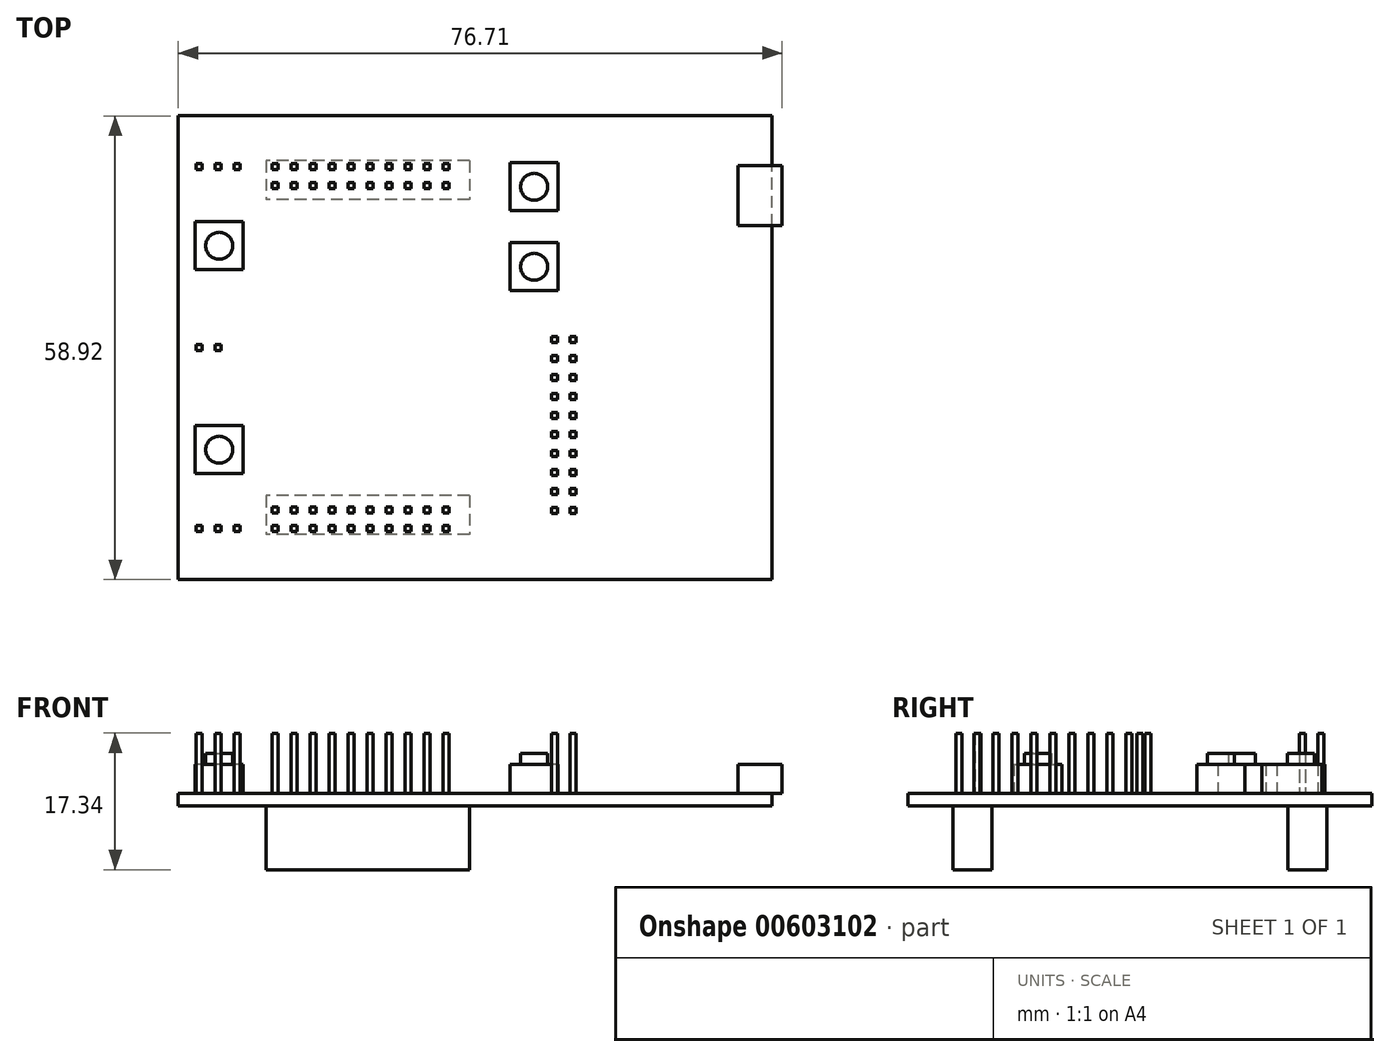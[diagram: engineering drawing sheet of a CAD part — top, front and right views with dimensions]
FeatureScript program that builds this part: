
annotation { "Feature Type Name" : "Feature", "Feature Type Description" : "" }
export const myFeature = defineFeature(function(context is Context, id is Id, definition is map)
    precondition{}
    {
        {
            var Q0;
            Q0=qCreatedBy(makeId("Top.planeOp"),FACE);
            var sketch = newSketch(context, id + "F0", { "sketchPlane" : qUnion([Q0])});
            skLineSegment(sketch, "E0.bottom", {"start": v(37.72, -29.46) * mm, "end": v(-37.72, -29.46) * mm});
            skLineSegment(sketch, "E0.top", {"start": v(37.72, 29.46) * mm, "end": v(-37.72, 29.46) * mm});
            skLineSegment(sketch, "E0.left", {"start": v(37.72, -29.46) * mm, "end": v(37.72, 29.46) * mm});
            skLineSegment(sketch, "E0.right", {"start": v(-37.72, -29.46) * mm, "end": v(-37.72, 29.46) * mm});
            skPoint(sketch, "E0.middle", {"position": v(0, 0) * mm});
            skSolve(sketch);
        }
        {
            var Q0;
            Q0 = qSketchRegion(id + "F0", true);
            extrude(context, id + "F1", {"entities" : qUnion([Q0]), "depth" : 1.59 * mm, "offsetDistance" : 25.4 * mm});
        }
        {
            var Q0;
            Q0=makeQuery(id+"F1.opExtrude","CAP_FACE",FACE,{"disambiguationData":[OSD([sQuery(id+"F0.wireOp",EDGE,"E0.bottom"),sQuery(id+"F0.wireOp",EDGE,"E0.top"),sQuery(id+"F0.wireOp",EDGE,"E0.left"),sQuery(id+"F0.wireOp",EDGE,"E0.right")])],"isStart":false});
            var sketch = newSketch(context, id + "F2", { "sketchPlane" : qUnion([Q0])});
            skLineSegment(sketch, "E1.bottom", {"start": v(33.5, 25.2) * mm, "end": v(39.96, 25.2) * mm});
            skLineSegment(sketch, "E1.top", {"start": v(33.5, 19.73) * mm, "end": v(39.96, 19.73) * mm});
            skLineSegment(sketch, "E1.left", {"start": v(33.5, 25.2) * mm, "end": v(33.5, 19.73) * mm});
            skLineSegment(sketch, "E1.right", {"start": v(39.96, 25.2) * mm, "end": v(39.96, 19.73) * mm});
            skLineSegment(sketch, "E2.bottom", {"start": v(26.18, 26.75) * mm, "end": v(29.14, 26.75) * mm});
            skLineSegment(sketch, "E2.top", {"start": v(26.18, 24.61) * mm, "end": v(29.14, 24.61) * mm});
            skLineSegment(sketch, "E2.left", {"start": v(26.18, 26.75) * mm, "end": v(26.18, 24.61) * mm});
            skLineSegment(sketch, "E2.right", {"start": v(29.14, 26.75) * mm, "end": v(29.14, 24.61) * mm});
            skLineSegment(sketch, "E3.bottom", {"start": v(9.92, -2.17) * mm, "end": v(12.87, -2.17) * mm});
            skLineSegment(sketch, "E3.top", {"start": v(9.92, -3.65) * mm, "end": v(12.87, -3.65) * mm});
            skLineSegment(sketch, "E3.left", {"start": v(9.92, -2.17) * mm, "end": v(9.92, -3.65) * mm});
            skLineSegment(sketch, "E3.right", {"start": v(12.87, -2.17) * mm, "end": v(12.87, -3.65) * mm});
            skLineSegment(sketch, "E4.bottom", {"start": v(-11.77, -11.37) * mm, "end": v(-7.83, -11.37) * mm});
            skLineSegment(sketch, "E4.top", {"start": v(-11.77, -12.85) * mm, "end": v(-7.83, -12.85) * mm});
            skLineSegment(sketch, "E4.left", {"start": v(-11.77, -11.37) * mm, "end": v(-11.77, -12.85) * mm});
            skLineSegment(sketch, "E4.right", {"start": v(-7.83, -11.37) * mm, "end": v(-7.83, -12.85) * mm});
            skLineSegment(sketch, "E5.bottom", {"start": v(-29.68, 12.3) * mm, "end": v(-28.37, 12.3) * mm});
            skLineSegment(sketch, "E5.top", {"start": v(-29.68, 8.84) * mm, "end": v(-28.37, 8.84) * mm});
            skLineSegment(sketch, "E5.left", {"start": v(-29.68, 12.3) * mm, "end": v(-29.68, 8.84) * mm});
            skLineSegment(sketch, "E5.right", {"start": v(-28.37, 12.3) * mm, "end": v(-28.37, 8.84) * mm});
            skLineSegment(sketch, "E6.bottom", {"start": v(-26.72, 14.1) * mm, "end": v(-21.63, 14.1) * mm});
            skLineSegment(sketch, "E6.top", {"start": v(-26.72, 15.9) * mm, "end": v(-21.63, 15.9) * mm});
            skLineSegment(sketch, "E6.left", {"start": v(-26.72, 14.1) * mm, "end": v(-26.72, 15.9) * mm});
            skLineSegment(sketch, "E6.right", {"start": v(-21.63, 14.1) * mm, "end": v(-21.63, 15.9) * mm});
            skSolve(sketch);
        }
        {
            var Q0;
            {var subQ0=sQuery(id+"F2.wireOp",EDGE,"E1.left");Q0=makeQuery(id+"F2.imprint","IMPRINT",FACE,{"disambiguationData":[TD([[makeQuery(id+"F2.imprint","IMPRINT",EDGE,{"derivedFrom":subQ0}),-1.0]])]});}
            var sketch = newSketch(context, id + "F3", { "sketchPlane" : qUnion([Q0])});
            skLineSegment(sketch, "E7.bottom", {"start": v(-12.95, -20.98) * mm, "end": v(-13.72, -20.98) * mm});
            skLineSegment(sketch, "E7.top", {"start": v(-12.95, -20.22) * mm, "end": v(-13.72, -20.22) * mm});
            skLineSegment(sketch, "E7.left", {"start": v(-12.95, -20.98) * mm, "end": v(-12.95, -20.22) * mm});
            skLineSegment(sketch, "E7.right", {"start": v(-13.72, -20.98) * mm, "end": v(-13.72, -20.22) * mm});
            skPoint(sketch, "E7.middle", {"position": v(-13.34, -20.6) * mm});
            skLineSegment(sketch, "E8.bottom", {"start": v(-15.37, -20.98) * mm, "end": v(-16.13, -20.98) * mm});
            skLineSegment(sketch, "E8.top", {"start": v(-15.37, -20.22) * mm, "end": v(-16.13, -20.22) * mm});
            skLineSegment(sketch, "E8.left", {"start": v(-15.37, -20.98) * mm, "end": v(-15.37, -20.22) * mm});
            skLineSegment(sketch, "E8.right", {"start": v(-16.13, -20.98) * mm, "end": v(-16.13, -20.22) * mm});
            skPoint(sketch, "E8.middle", {"position": v(-15.75, -20.6) * mm});
            skLineSegment(sketch, "E9.bottom", {"start": v(-17.78, -20.98) * mm, "end": v(-18.54, -20.98) * mm});
            skLineSegment(sketch, "E9.top", {"start": v(-17.78, -20.22) * mm, "end": v(-18.54, -20.22) * mm});
            skLineSegment(sketch, "E9.left", {"start": v(-17.78, -20.98) * mm, "end": v(-17.78, -20.22) * mm});
            skLineSegment(sketch, "E9.right", {"start": v(-18.54, -20.98) * mm, "end": v(-18.54, -20.22) * mm});
            skPoint(sketch, "E9.middle", {"position": v(-18.16, -20.6) * mm});
            skLineSegment(sketch, "E10.bottom", {"start": v(-20.2, -20.98) * mm, "end": v(-20.96, -20.98) * mm});
            skLineSegment(sketch, "E10.top", {"start": v(-20.2, -20.22) * mm, "end": v(-20.96, -20.22) * mm});
            skLineSegment(sketch, "E10.left", {"start": v(-20.2, -20.98) * mm, "end": v(-20.2, -20.22) * mm});
            skLineSegment(sketch, "E10.right", {"start": v(-20.96, -20.98) * mm, "end": v(-20.96, -20.22) * mm});
            skPoint(sketch, "E10.middle", {"position": v(-20.57, -20.6) * mm});
            skLineSegment(sketch, "E11.bottom", {"start": v(-22.6, -20.98) * mm, "end": v(-23.37, -20.98) * mm});
            skLineSegment(sketch, "E11.top", {"start": v(-22.6, -20.22) * mm, "end": v(-23.37, -20.22) * mm});
            skLineSegment(sketch, "E11.left", {"start": v(-22.6, -20.98) * mm, "end": v(-22.6, -20.22) * mm});
            skLineSegment(sketch, "E11.right", {"start": v(-23.37, -20.98) * mm, "end": v(-23.37, -20.22) * mm});
            skPoint(sketch, "E11.middle", {"position": v(-22.99, -20.6) * mm});
            skLineSegment(sketch, "E12.bottom", {"start": v(-25.02, -20.98) * mm, "end": v(-25.78, -20.98) * mm});
            skLineSegment(sketch, "E12.top", {"start": v(-25.02, -20.22) * mm, "end": v(-25.78, -20.22) * mm});
            skLineSegment(sketch, "E12.left", {"start": v(-25.02, -20.98) * mm, "end": v(-25.02, -20.22) * mm});
            skLineSegment(sketch, "E12.right", {"start": v(-25.78, -20.98) * mm, "end": v(-25.78, -20.22) * mm});
            skPoint(sketch, "E12.middle", {"position": v(-25.4, -20.6) * mm});
            skLineSegment(sketch, "E13.bottom", {"start": v(-10.54, -20.98) * mm, "end": v(-11.3, -20.98) * mm});
            skLineSegment(sketch, "E13.top", {"start": v(-10.54, -20.22) * mm, "end": v(-11.3, -20.22) * mm});
            skLineSegment(sketch, "E13.left", {"start": v(-10.54, -20.98) * mm, "end": v(-10.54, -20.22) * mm});
            skLineSegment(sketch, "E13.right", {"start": v(-11.3, -20.98) * mm, "end": v(-11.3, -20.22) * mm});
            skPoint(sketch, "E13.middle", {"position": v(-10.92, -20.6) * mm});
            skLineSegment(sketch, "E14.bottom", {"start": v(-8.13, -20.98) * mm, "end": v(-8.9, -20.98) * mm});
            skLineSegment(sketch, "E14.top", {"start": v(-8.13, -20.22) * mm, "end": v(-8.9, -20.22) * mm});
            skLineSegment(sketch, "E14.left", {"start": v(-8.13, -20.98) * mm, "end": v(-8.13, -20.22) * mm});
            skLineSegment(sketch, "E14.right", {"start": v(-8.9, -20.98) * mm, "end": v(-8.9, -20.22) * mm});
            skPoint(sketch, "E14.middle", {"position": v(-8.5, -20.6) * mm});
            skLineSegment(sketch, "E15.bottom", {"start": v(-5.72, -20.98) * mm, "end": v(-6.48, -20.98) * mm});
            skLineSegment(sketch, "E15.top", {"start": v(-5.72, -20.22) * mm, "end": v(-6.48, -20.22) * mm});
            skLineSegment(sketch, "E15.left", {"start": v(-5.72, -20.98) * mm, "end": v(-5.72, -20.22) * mm});
            skLineSegment(sketch, "E15.right", {"start": v(-6.48, -20.98) * mm, "end": v(-6.48, -20.22) * mm});
            skPoint(sketch, "E15.middle", {"position": v(-6.1, -20.6) * mm});
            skLineSegment(sketch, "E16.bottom", {"start": v(-3.3, -20.98) * mm, "end": v(-4.06, -20.98) * mm});
            skLineSegment(sketch, "E16.top", {"start": v(-3.3, -20.22) * mm, "end": v(-4.06, -20.22) * mm});
            skLineSegment(sketch, "E16.left", {"start": v(-3.3, -20.98) * mm, "end": v(-3.3, -20.22) * mm});
            skLineSegment(sketch, "E16.right", {"start": v(-4.06, -20.98) * mm, "end": v(-4.06, -20.22) * mm});
            skPoint(sketch, "E16.middle", {"position": v(-3.68, -20.6) * mm});
            skLineSegment(sketch, "E17.bottom", {"start": v(-12.95, -23.37) * mm, "end": v(-13.72, -23.37) * mm});
            skLineSegment(sketch, "E17.top", {"start": v(-12.95, -22.6) * mm, "end": v(-13.72, -22.6) * mm});
            skLineSegment(sketch, "E17.left", {"start": v(-12.95, -23.37) * mm, "end": v(-12.95, -22.6) * mm});
            skLineSegment(sketch, "E17.right", {"start": v(-13.72, -23.37) * mm, "end": v(-13.72, -22.6) * mm});
            skPoint(sketch, "E17.middle", {"position": v(-13.34, -22.99) * mm});
            skLineSegment(sketch, "E18.bottom", {"start": v(-15.37, -23.37) * mm, "end": v(-16.13, -23.37) * mm});
            skLineSegment(sketch, "E18.top", {"start": v(-15.37, -22.6) * mm, "end": v(-16.13, -22.6) * mm});
            skLineSegment(sketch, "E18.left", {"start": v(-15.37, -23.37) * mm, "end": v(-15.37, -22.6) * mm});
            skLineSegment(sketch, "E18.right", {"start": v(-16.13, -23.37) * mm, "end": v(-16.13, -22.6) * mm});
            skPoint(sketch, "E18.middle", {"position": v(-15.75, -22.99) * mm});
            skLineSegment(sketch, "E19.bottom", {"start": v(-17.78, -23.37) * mm, "end": v(-18.54, -23.37) * mm});
            skLineSegment(sketch, "E19.top", {"start": v(-17.78, -22.6) * mm, "end": v(-18.54, -22.6) * mm});
            skLineSegment(sketch, "E19.left", {"start": v(-17.78, -23.37) * mm, "end": v(-17.78, -22.6) * mm});
            skLineSegment(sketch, "E19.right", {"start": v(-18.54, -23.37) * mm, "end": v(-18.54, -22.6) * mm});
            skPoint(sketch, "E19.middle", {"position": v(-18.16, -22.99) * mm});
            skLineSegment(sketch, "E20.bottom", {"start": v(-20.2, -23.37) * mm, "end": v(-20.96, -23.37) * mm});
            skLineSegment(sketch, "E20.top", {"start": v(-20.2, -22.6) * mm, "end": v(-20.96, -22.6) * mm});
            skLineSegment(sketch, "E20.left", {"start": v(-20.2, -23.37) * mm, "end": v(-20.2, -22.6) * mm});
            skLineSegment(sketch, "E20.right", {"start": v(-20.96, -23.37) * mm, "end": v(-20.96, -22.6) * mm});
            skPoint(sketch, "E20.middle", {"position": v(-20.57, -22.99) * mm});
            skLineSegment(sketch, "E21.bottom", {"start": v(-22.6, -23.37) * mm, "end": v(-23.37, -23.37) * mm});
            skLineSegment(sketch, "E21.top", {"start": v(-22.6, -22.6) * mm, "end": v(-23.37, -22.6) * mm});
            skLineSegment(sketch, "E21.left", {"start": v(-22.6, -23.37) * mm, "end": v(-22.6, -22.6) * mm});
            skLineSegment(sketch, "E21.right", {"start": v(-23.37, -23.37) * mm, "end": v(-23.37, -22.6) * mm});
            skPoint(sketch, "E21.middle", {"position": v(-22.99, -22.99) * mm});
            skLineSegment(sketch, "E22.bottom", {"start": v(-25.02, -23.37) * mm, "end": v(-25.78, -23.37) * mm});
            skLineSegment(sketch, "E22.top", {"start": v(-25.02, -22.6) * mm, "end": v(-25.78, -22.6) * mm});
            skLineSegment(sketch, "E22.left", {"start": v(-25.02, -23.37) * mm, "end": v(-25.02, -22.6) * mm});
            skLineSegment(sketch, "E22.right", {"start": v(-25.78, -23.37) * mm, "end": v(-25.78, -22.6) * mm});
            skPoint(sketch, "E22.middle", {"position": v(-25.4, -22.99) * mm});
            skLineSegment(sketch, "E23.bottom", {"start": v(-10.54, -23.37) * mm, "end": v(-11.3, -23.37) * mm});
            skLineSegment(sketch, "E23.top", {"start": v(-10.54, -22.6) * mm, "end": v(-11.3, -22.6) * mm});
            skLineSegment(sketch, "E23.left", {"start": v(-10.54, -23.37) * mm, "end": v(-10.54, -22.6) * mm});
            skLineSegment(sketch, "E23.right", {"start": v(-11.3, -23.37) * mm, "end": v(-11.3, -22.6) * mm});
            skPoint(sketch, "E23.middle", {"position": v(-10.92, -22.99) * mm});
            skLineSegment(sketch, "E24.bottom", {"start": v(-8.13, -23.37) * mm, "end": v(-8.9, -23.37) * mm});
            skLineSegment(sketch, "E24.top", {"start": v(-8.13, -22.6) * mm, "end": v(-8.9, -22.6) * mm});
            skLineSegment(sketch, "E24.left", {"start": v(-8.13, -23.37) * mm, "end": v(-8.13, -22.6) * mm});
            skLineSegment(sketch, "E24.right", {"start": v(-8.9, -23.37) * mm, "end": v(-8.9, -22.6) * mm});
            skPoint(sketch, "E24.middle", {"position": v(-8.5, -22.99) * mm});
            skLineSegment(sketch, "E25.bottom", {"start": v(-5.72, -23.37) * mm, "end": v(-6.48, -23.37) * mm});
            skLineSegment(sketch, "E25.top", {"start": v(-5.72, -22.6) * mm, "end": v(-6.48, -22.6) * mm});
            skLineSegment(sketch, "E25.left", {"start": v(-5.72, -23.37) * mm, "end": v(-5.72, -22.6) * mm});
            skLineSegment(sketch, "E25.right", {"start": v(-6.48, -23.37) * mm, "end": v(-6.48, -22.6) * mm});
            skPoint(sketch, "E25.middle", {"position": v(-6.1, -22.99) * mm});
            skLineSegment(sketch, "E26.bottom", {"start": v(-3.3, -23.37) * mm, "end": v(-4.06, -23.37) * mm});
            skLineSegment(sketch, "E26.top", {"start": v(-3.3, -22.6) * mm, "end": v(-4.06, -22.6) * mm});
            skLineSegment(sketch, "E26.left", {"start": v(-3.3, -23.37) * mm, "end": v(-3.3, -22.6) * mm});
            skLineSegment(sketch, "E26.right", {"start": v(-4.06, -23.37) * mm, "end": v(-4.06, -22.6) * mm});
            skPoint(sketch, "E26.middle", {"position": v(-3.68, -22.99) * mm});
            skLineSegment(sketch, "E27.bottom", {"start": v(-12.95, 22.6) * mm, "end": v(-13.72, 22.6) * mm});
            skLineSegment(sketch, "E27.top", {"start": v(-12.95, 23.37) * mm, "end": v(-13.72, 23.37) * mm});
            skLineSegment(sketch, "E27.left", {"start": v(-12.95, 22.6) * mm, "end": v(-12.95, 23.37) * mm});
            skLineSegment(sketch, "E27.right", {"start": v(-13.72, 22.6) * mm, "end": v(-13.72, 23.37) * mm});
            skPoint(sketch, "E27.middle", {"position": v(-13.34, 22.99) * mm});
            skLineSegment(sketch, "E28.bottom", {"start": v(-15.37, 22.6) * mm, "end": v(-16.13, 22.6) * mm});
            skLineSegment(sketch, "E28.top", {"start": v(-15.37, 23.37) * mm, "end": v(-16.13, 23.37) * mm});
            skLineSegment(sketch, "E28.left", {"start": v(-15.37, 22.6) * mm, "end": v(-15.37, 23.37) * mm});
            skLineSegment(sketch, "E28.right", {"start": v(-16.13, 22.6) * mm, "end": v(-16.13, 23.37) * mm});
            skPoint(sketch, "E28.middle", {"position": v(-15.75, 22.99) * mm});
            skLineSegment(sketch, "E29.bottom", {"start": v(-17.78, 22.6) * mm, "end": v(-18.54, 22.6) * mm});
            skLineSegment(sketch, "E29.top", {"start": v(-17.78, 23.37) * mm, "end": v(-18.54, 23.37) * mm});
            skLineSegment(sketch, "E29.left", {"start": v(-17.78, 22.6) * mm, "end": v(-17.78, 23.37) * mm});
            skLineSegment(sketch, "E29.right", {"start": v(-18.54, 22.6) * mm, "end": v(-18.54, 23.37) * mm});
            skPoint(sketch, "E29.middle", {"position": v(-18.16, 22.99) * mm});
            skLineSegment(sketch, "E30.bottom", {"start": v(-20.2, 22.6) * mm, "end": v(-20.96, 22.6) * mm});
            skLineSegment(sketch, "E30.top", {"start": v(-20.2, 23.37) * mm, "end": v(-20.96, 23.37) * mm});
            skLineSegment(sketch, "E30.left", {"start": v(-20.2, 22.6) * mm, "end": v(-20.2, 23.37) * mm});
            skLineSegment(sketch, "E30.right", {"start": v(-20.96, 22.6) * mm, "end": v(-20.96, 23.37) * mm});
            skPoint(sketch, "E30.middle", {"position": v(-20.57, 22.99) * mm});
            skLineSegment(sketch, "E31.bottom", {"start": v(-22.6, 22.6) * mm, "end": v(-23.37, 22.6) * mm});
            skLineSegment(sketch, "E31.top", {"start": v(-22.6, 23.37) * mm, "end": v(-23.37, 23.37) * mm});
            skLineSegment(sketch, "E31.left", {"start": v(-22.6, 22.6) * mm, "end": v(-22.6, 23.37) * mm});
            skLineSegment(sketch, "E31.right", {"start": v(-23.37, 22.6) * mm, "end": v(-23.37, 23.37) * mm});
            skPoint(sketch, "E31.middle", {"position": v(-22.99, 22.99) * mm});
            skLineSegment(sketch, "E32.bottom", {"start": v(-25.02, 22.6) * mm, "end": v(-25.78, 22.6) * mm});
            skLineSegment(sketch, "E32.top", {"start": v(-25.02, 23.37) * mm, "end": v(-25.78, 23.37) * mm});
            skLineSegment(sketch, "E32.left", {"start": v(-25.02, 22.6) * mm, "end": v(-25.02, 23.37) * mm});
            skLineSegment(sketch, "E32.right", {"start": v(-25.78, 22.6) * mm, "end": v(-25.78, 23.37) * mm});
            skPoint(sketch, "E32.middle", {"position": v(-25.4, 22.99) * mm});
            skLineSegment(sketch, "E33.bottom", {"start": v(-10.54, 22.6) * mm, "end": v(-11.3, 22.6) * mm});
            skLineSegment(sketch, "E33.top", {"start": v(-10.54, 23.37) * mm, "end": v(-11.3, 23.37) * mm});
            skLineSegment(sketch, "E33.left", {"start": v(-10.54, 22.6) * mm, "end": v(-10.54, 23.37) * mm});
            skLineSegment(sketch, "E33.right", {"start": v(-11.3, 22.6) * mm, "end": v(-11.3, 23.37) * mm});
            skPoint(sketch, "E33.middle", {"position": v(-10.92, 22.99) * mm});
            skLineSegment(sketch, "E34.bottom", {"start": v(-8.13, 22.6) * mm, "end": v(-8.9, 22.6) * mm});
            skLineSegment(sketch, "E34.top", {"start": v(-8.13, 23.37) * mm, "end": v(-8.9, 23.37) * mm});
            skLineSegment(sketch, "E34.left", {"start": v(-8.13, 22.6) * mm, "end": v(-8.13, 23.37) * mm});
            skLineSegment(sketch, "E34.right", {"start": v(-8.9, 22.6) * mm, "end": v(-8.9, 23.37) * mm});
            skPoint(sketch, "E34.middle", {"position": v(-8.5, 22.99) * mm});
            skLineSegment(sketch, "E35.bottom", {"start": v(-5.72, 22.6) * mm, "end": v(-6.48, 22.6) * mm});
            skLineSegment(sketch, "E35.top", {"start": v(-5.72, 23.37) * mm, "end": v(-6.48, 23.37) * mm});
            skLineSegment(sketch, "E35.left", {"start": v(-5.72, 22.6) * mm, "end": v(-5.72, 23.37) * mm});
            skLineSegment(sketch, "E35.right", {"start": v(-6.48, 22.6) * mm, "end": v(-6.48, 23.37) * mm});
            skPoint(sketch, "E35.middle", {"position": v(-6.1, 22.99) * mm});
            skLineSegment(sketch, "E36.bottom", {"start": v(-3.3, 22.6) * mm, "end": v(-4.06, 22.6) * mm});
            skLineSegment(sketch, "E36.top", {"start": v(-3.3, 23.37) * mm, "end": v(-4.06, 23.37) * mm});
            skLineSegment(sketch, "E36.left", {"start": v(-3.3, 22.6) * mm, "end": v(-3.3, 23.37) * mm});
            skLineSegment(sketch, "E36.right", {"start": v(-4.06, 22.6) * mm, "end": v(-4.06, 23.37) * mm});
            skPoint(sketch, "E36.middle", {"position": v(-3.68, 22.99) * mm});
            skLineSegment(sketch, "E37.bottom", {"start": v(-12.95, 20.22) * mm, "end": v(-13.72, 20.22) * mm});
            skLineSegment(sketch, "E37.top", {"start": v(-12.95, 20.98) * mm, "end": v(-13.72, 20.98) * mm});
            skLineSegment(sketch, "E37.left", {"start": v(-12.95, 20.22) * mm, "end": v(-12.95, 20.98) * mm});
            skLineSegment(sketch, "E37.right", {"start": v(-13.72, 20.22) * mm, "end": v(-13.72, 20.98) * mm});
            skPoint(sketch, "E37.middle", {"position": v(-13.34, 20.6) * mm});
            skLineSegment(sketch, "E38.bottom", {"start": v(-15.37, 20.22) * mm, "end": v(-16.13, 20.22) * mm});
            skLineSegment(sketch, "E38.top", {"start": v(-15.37, 20.98) * mm, "end": v(-16.13, 20.98) * mm});
            skLineSegment(sketch, "E38.left", {"start": v(-15.37, 20.22) * mm, "end": v(-15.37, 20.98) * mm});
            skLineSegment(sketch, "E38.right", {"start": v(-16.13, 20.22) * mm, "end": v(-16.13, 20.98) * mm});
            skPoint(sketch, "E38.middle", {"position": v(-15.75, 20.6) * mm});
            skLineSegment(sketch, "E39.bottom", {"start": v(-17.78, 20.22) * mm, "end": v(-18.54, 20.22) * mm});
            skLineSegment(sketch, "E39.top", {"start": v(-17.78, 20.98) * mm, "end": v(-18.54, 20.98) * mm});
            skLineSegment(sketch, "E39.left", {"start": v(-17.78, 20.22) * mm, "end": v(-17.78, 20.98) * mm});
            skLineSegment(sketch, "E39.right", {"start": v(-18.54, 20.22) * mm, "end": v(-18.54, 20.98) * mm});
            skPoint(sketch, "E39.middle", {"position": v(-18.16, 20.6) * mm});
            skLineSegment(sketch, "E40.bottom", {"start": v(-20.2, 20.22) * mm, "end": v(-20.96, 20.22) * mm});
            skLineSegment(sketch, "E40.top", {"start": v(-20.2, 20.98) * mm, "end": v(-20.96, 20.98) * mm});
            skLineSegment(sketch, "E40.left", {"start": v(-20.2, 20.22) * mm, "end": v(-20.2, 20.98) * mm});
            skLineSegment(sketch, "E40.right", {"start": v(-20.96, 20.22) * mm, "end": v(-20.96, 20.98) * mm});
            skPoint(sketch, "E40.middle", {"position": v(-20.57, 20.6) * mm});
            skLineSegment(sketch, "E41.bottom", {"start": v(-22.6, 20.22) * mm, "end": v(-23.37, 20.22) * mm});
            skLineSegment(sketch, "E41.top", {"start": v(-22.6, 20.98) * mm, "end": v(-23.37, 20.98) * mm});
            skLineSegment(sketch, "E41.left", {"start": v(-22.6, 20.22) * mm, "end": v(-22.6, 20.98) * mm});
            skLineSegment(sketch, "E41.right", {"start": v(-23.37, 20.22) * mm, "end": v(-23.37, 20.98) * mm});
            skPoint(sketch, "E41.middle", {"position": v(-22.99, 20.6) * mm});
            skLineSegment(sketch, "E42.bottom", {"start": v(-25.02, 20.22) * mm, "end": v(-25.78, 20.22) * mm});
            skLineSegment(sketch, "E42.top", {"start": v(-25.02, 20.98) * mm, "end": v(-25.78, 20.98) * mm});
            skLineSegment(sketch, "E42.left", {"start": v(-25.02, 20.22) * mm, "end": v(-25.02, 20.98) * mm});
            skLineSegment(sketch, "E42.right", {"start": v(-25.78, 20.22) * mm, "end": v(-25.78, 20.98) * mm});
            skPoint(sketch, "E42.middle", {"position": v(-25.4, 20.6) * mm});
            skLineSegment(sketch, "E43.bottom", {"start": v(-10.54, 20.22) * mm, "end": v(-11.3, 20.22) * mm});
            skLineSegment(sketch, "E43.top", {"start": v(-10.54, 20.98) * mm, "end": v(-11.3, 20.98) * mm});
            skLineSegment(sketch, "E43.left", {"start": v(-10.54, 20.22) * mm, "end": v(-10.54, 20.98) * mm});
            skLineSegment(sketch, "E43.right", {"start": v(-11.3, 20.22) * mm, "end": v(-11.3, 20.98) * mm});
            skPoint(sketch, "E43.middle", {"position": v(-10.92, 20.6) * mm});
            skLineSegment(sketch, "E44.bottom", {"start": v(-8.13, 20.22) * mm, "end": v(-8.9, 20.22) * mm});
            skLineSegment(sketch, "E44.top", {"start": v(-8.13, 20.98) * mm, "end": v(-8.9, 20.98) * mm});
            skLineSegment(sketch, "E44.left", {"start": v(-8.13, 20.22) * mm, "end": v(-8.13, 20.98) * mm});
            skLineSegment(sketch, "E44.right", {"start": v(-8.9, 20.22) * mm, "end": v(-8.9, 20.98) * mm});
            skPoint(sketch, "E44.middle", {"position": v(-8.5, 20.6) * mm});
            skLineSegment(sketch, "E45.bottom", {"start": v(-5.72, 20.22) * mm, "end": v(-6.48, 20.22) * mm});
            skLineSegment(sketch, "E45.top", {"start": v(-5.72, 20.98) * mm, "end": v(-6.48, 20.98) * mm});
            skLineSegment(sketch, "E45.left", {"start": v(-5.72, 20.22) * mm, "end": v(-5.72, 20.98) * mm});
            skLineSegment(sketch, "E45.right", {"start": v(-6.48, 20.22) * mm, "end": v(-6.48, 20.98) * mm});
            skPoint(sketch, "E45.middle", {"position": v(-6.1, 20.6) * mm});
            skLineSegment(sketch, "E46.bottom", {"start": v(-3.3, 20.22) * mm, "end": v(-4.06, 20.22) * mm});
            skLineSegment(sketch, "E46.top", {"start": v(-3.3, 20.98) * mm, "end": v(-4.06, 20.98) * mm});
            skLineSegment(sketch, "E46.left", {"start": v(-3.3, 20.22) * mm, "end": v(-3.3, 20.98) * mm});
            skLineSegment(sketch, "E46.right", {"start": v(-4.06, 20.22) * mm, "end": v(-4.06, 20.98) * mm});
            skPoint(sketch, "E46.middle", {"position": v(-3.68, 20.6) * mm});
            skLineSegment(sketch, "E47.bottom", {"start": v(12.07, -11.43) * mm, "end": v(12.07, -10.67) * mm});
            skLineSegment(sketch, "E47.top", {"start": v(12.83, -11.43) * mm, "end": v(12.83, -10.67) * mm});
            skLineSegment(sketch, "E47.left", {"start": v(12.07, -11.43) * mm, "end": v(12.83, -11.43) * mm});
            skLineSegment(sketch, "E47.right", {"start": v(12.07, -10.67) * mm, "end": v(12.83, -10.67) * mm});
            skPoint(sketch, "E47.middle", {"position": v(12.45, -11.05) * mm});
            skLineSegment(sketch, "E48.bottom", {"start": v(12.07, -9.02) * mm, "end": v(12.07, -8.26) * mm});
            skLineSegment(sketch, "E48.top", {"start": v(12.83, -9.02) * mm, "end": v(12.83, -8.25) * mm});
            skLineSegment(sketch, "E48.left", {"start": v(12.07, -9.02) * mm, "end": v(12.83, -9.02) * mm});
            skLineSegment(sketch, "E48.right", {"start": v(12.07, -8.25) * mm, "end": v(12.83, -8.25) * mm});
            skPoint(sketch, "E48.middle", {"position": v(12.45, -8.64) * mm});
            skLineSegment(sketch, "E49.bottom", {"start": v(12.07, -6.6) * mm, "end": v(12.07, -5.84) * mm});
            skLineSegment(sketch, "E49.top", {"start": v(12.83, -6.6) * mm, "end": v(12.83, -5.84) * mm});
            skLineSegment(sketch, "E49.left", {"start": v(12.07, -6.6) * mm, "end": v(12.83, -6.6) * mm});
            skLineSegment(sketch, "E49.right", {"start": v(12.07, -5.84) * mm, "end": v(12.83, -5.84) * mm});
            skPoint(sketch, "E49.middle", {"position": v(12.45, -6.22) * mm});
            skLineSegment(sketch, "E50.bottom", {"start": v(12.07, -4.2) * mm, "end": v(12.07, -3.43) * mm});
            skLineSegment(sketch, "E50.top", {"start": v(12.83, -4.2) * mm, "end": v(12.83, -3.43) * mm});
            skLineSegment(sketch, "E50.left", {"start": v(12.07, -4.2) * mm, "end": v(12.83, -4.2) * mm});
            skLineSegment(sketch, "E50.right", {"start": v(12.07, -3.43) * mm, "end": v(12.83, -3.43) * mm});
            skPoint(sketch, "E50.middle", {"position": v(12.45, -3.81) * mm});
            skLineSegment(sketch, "E51.bottom", {"start": v(12.07, -1.78) * mm, "end": v(12.07, -1.02) * mm});
            skLineSegment(sketch, "E51.top", {"start": v(12.83, -1.78) * mm, "end": v(12.83, -1.02) * mm});
            skLineSegment(sketch, "E51.left", {"start": v(12.07, -1.78) * mm, "end": v(12.83, -1.78) * mm});
            skLineSegment(sketch, "E51.right", {"start": v(12.07, -1.02) * mm, "end": v(12.83, -1.02) * mm});
            skPoint(sketch, "E51.middle", {"position": v(12.45, -1.4) * mm});
            skLineSegment(sketch, "E52.bottom", {"start": v(12.07, 0.63) * mm, "end": v(12.07, 1.4) * mm});
            skLineSegment(sketch, "E52.top", {"start": v(12.83, 0.63) * mm, "end": v(12.83, 1.4) * mm});
            skLineSegment(sketch, "E52.left", {"start": v(12.07, 0.63) * mm, "end": v(12.83, 0.63) * mm});
            skLineSegment(sketch, "E52.right", {"start": v(12.07, 1.4) * mm, "end": v(12.83, 1.4) * mm});
            skPoint(sketch, "E52.middle", {"position": v(12.45, 1.02) * mm});
            skLineSegment(sketch, "E53.bottom", {"start": v(12.07, -13.84) * mm, "end": v(12.07, -13.08) * mm});
            skLineSegment(sketch, "E53.top", {"start": v(12.83, -13.84) * mm, "end": v(12.83, -13.08) * mm});
            skLineSegment(sketch, "E53.left", {"start": v(12.07, -13.84) * mm, "end": v(12.83, -13.84) * mm});
            skLineSegment(sketch, "E53.right", {"start": v(12.07, -13.08) * mm, "end": v(12.83, -13.08) * mm});
            skPoint(sketch, "E53.middle", {"position": v(12.45, -13.46) * mm});
            skLineSegment(sketch, "E54.bottom", {"start": v(12.07, -16.26) * mm, "end": v(12.07, -15.5) * mm});
            skLineSegment(sketch, "E54.top", {"start": v(12.83, -16.26) * mm, "end": v(12.83, -15.5) * mm});
            skLineSegment(sketch, "E54.left", {"start": v(12.07, -16.26) * mm, "end": v(12.83, -16.26) * mm});
            skLineSegment(sketch, "E54.right", {"start": v(12.07, -15.5) * mm, "end": v(12.83, -15.5) * mm});
            skPoint(sketch, "E54.middle", {"position": v(12.45, -15.88) * mm});
            skLineSegment(sketch, "E55.bottom", {"start": v(12.07, -18.67) * mm, "end": v(12.07, -17.9) * mm});
            skLineSegment(sketch, "E55.top", {"start": v(12.83, -18.67) * mm, "end": v(12.83, -17.9) * mm});
            skLineSegment(sketch, "E55.left", {"start": v(12.07, -18.67) * mm, "end": v(12.83, -18.67) * mm});
            skLineSegment(sketch, "E55.right", {"start": v(12.07, -17.9) * mm, "end": v(12.83, -17.9) * mm});
            skPoint(sketch, "E55.middle", {"position": v(12.45, -18.29) * mm});
            skLineSegment(sketch, "E56.bottom", {"start": v(12.07, -21.08) * mm, "end": v(12.07, -20.32) * mm});
            skLineSegment(sketch, "E56.top", {"start": v(12.83, -21.08) * mm, "end": v(12.83, -20.32) * mm});
            skLineSegment(sketch, "E56.left", {"start": v(12.07, -21.08) * mm, "end": v(12.83, -21.08) * mm});
            skLineSegment(sketch, "E56.right", {"start": v(12.07, -20.32) * mm, "end": v(12.83, -20.32) * mm});
            skPoint(sketch, "E56.middle", {"position": v(12.45, -20.7) * mm});
            skLineSegment(sketch, "E57.bottom", {"start": v(9.68, -11.43) * mm, "end": v(9.68, -10.67) * mm});
            skLineSegment(sketch, "E57.top", {"start": v(10.44, -11.43) * mm, "end": v(10.44, -10.67) * mm});
            skLineSegment(sketch, "E57.left", {"start": v(9.68, -11.43) * mm, "end": v(10.44, -11.43) * mm});
            skLineSegment(sketch, "E57.right", {"start": v(9.68, -10.67) * mm, "end": v(10.44, -10.67) * mm});
            skPoint(sketch, "E57.middle", {"position": v(10.06, -11.05) * mm});
            skLineSegment(sketch, "E58.bottom", {"start": v(9.68, -9.02) * mm, "end": v(9.68, -8.25) * mm});
            skLineSegment(sketch, "E58.top", {"start": v(10.44, -9.02) * mm, "end": v(10.44, -8.25) * mm});
            skLineSegment(sketch, "E58.left", {"start": v(9.68, -9.02) * mm, "end": v(10.44, -9.02) * mm});
            skLineSegment(sketch, "E58.right", {"start": v(9.68, -8.25) * mm, "end": v(10.44, -8.25) * mm});
            skPoint(sketch, "E58.middle", {"position": v(10.06, -8.64) * mm});
            skLineSegment(sketch, "E59.bottom", {"start": v(9.68, -6.6) * mm, "end": v(9.68, -5.84) * mm});
            skLineSegment(sketch, "E59.top", {"start": v(10.44, -6.6) * mm, "end": v(10.44, -5.84) * mm});
            skLineSegment(sketch, "E59.left", {"start": v(9.68, -6.6) * mm, "end": v(10.44, -6.6) * mm});
            skLineSegment(sketch, "E59.right", {"start": v(9.68, -5.84) * mm, "end": v(10.44, -5.84) * mm});
            skPoint(sketch, "E59.middle", {"position": v(10.06, -6.22) * mm});
            skLineSegment(sketch, "E60.bottom", {"start": v(9.68, -4.2) * mm, "end": v(9.68, -3.43) * mm});
            skLineSegment(sketch, "E60.top", {"start": v(10.44, -4.2) * mm, "end": v(10.44, -3.43) * mm});
            skLineSegment(sketch, "E60.left", {"start": v(9.68, -4.2) * mm, "end": v(10.44, -4.2) * mm});
            skLineSegment(sketch, "E60.right", {"start": v(9.68, -3.43) * mm, "end": v(10.44, -3.43) * mm});
            skPoint(sketch, "E60.middle", {"position": v(10.06, -3.8) * mm});
            skLineSegment(sketch, "E61.bottom", {"start": v(9.68, -1.78) * mm, "end": v(9.68, -1.02) * mm});
            skLineSegment(sketch, "E61.top", {"start": v(10.44, -1.78) * mm, "end": v(10.44, -1.02) * mm});
            skLineSegment(sketch, "E61.left", {"start": v(9.68, -1.78) * mm, "end": v(10.44, -1.78) * mm});
            skLineSegment(sketch, "E61.right", {"start": v(9.68, -1.02) * mm, "end": v(10.44, -1.02) * mm});
            skPoint(sketch, "E61.middle", {"position": v(10.06, -1.4) * mm});
            skLineSegment(sketch, "E62.bottom", {"start": v(9.68, 0.64) * mm, "end": v(9.68, 1.4) * mm});
            skLineSegment(sketch, "E62.top", {"start": v(10.44, 0.64) * mm, "end": v(10.44, 1.4) * mm});
            skLineSegment(sketch, "E62.left", {"start": v(9.68, 0.64) * mm, "end": v(10.44, 0.64) * mm});
            skLineSegment(sketch, "E62.right", {"start": v(9.68, 1.4) * mm, "end": v(10.44, 1.4) * mm});
            skPoint(sketch, "E62.middle", {"position": v(10.06, 1.02) * mm});
            skLineSegment(sketch, "E63.bottom", {"start": v(9.68, -13.84) * mm, "end": v(9.68, -13.08) * mm});
            skLineSegment(sketch, "E63.top", {"start": v(10.44, -13.84) * mm, "end": v(10.44, -13.08) * mm});
            skLineSegment(sketch, "E63.left", {"start": v(9.68, -13.84) * mm, "end": v(10.44, -13.84) * mm});
            skLineSegment(sketch, "E63.right", {"start": v(9.68, -13.08) * mm, "end": v(10.44, -13.08) * mm});
            skPoint(sketch, "E63.middle", {"position": v(10.06, -13.46) * mm});
            skLineSegment(sketch, "E64.bottom", {"start": v(9.68, -16.26) * mm, "end": v(9.68, -15.5) * mm});
            skLineSegment(sketch, "E64.top", {"start": v(10.44, -16.26) * mm, "end": v(10.44, -15.5) * mm});
            skLineSegment(sketch, "E64.left", {"start": v(9.68, -16.26) * mm, "end": v(10.44, -16.26) * mm});
            skLineSegment(sketch, "E64.right", {"start": v(9.68, -15.5) * mm, "end": v(10.44, -15.5) * mm});
            skPoint(sketch, "E64.middle", {"position": v(10.06, -15.87) * mm});
            skLineSegment(sketch, "E65.bottom", {"start": v(9.68, -18.67) * mm, "end": v(9.68, -17.9) * mm});
            skLineSegment(sketch, "E65.top", {"start": v(10.44, -18.67) * mm, "end": v(10.44, -17.9) * mm});
            skLineSegment(sketch, "E65.left", {"start": v(9.68, -18.67) * mm, "end": v(10.44, -18.67) * mm});
            skLineSegment(sketch, "E65.right", {"start": v(9.68, -17.9) * mm, "end": v(10.44, -17.9) * mm});
            skPoint(sketch, "E65.middle", {"position": v(10.06, -18.29) * mm});
            skLineSegment(sketch, "E66.bottom", {"start": v(9.68, -21.08) * mm, "end": v(9.68, -20.32) * mm});
            skLineSegment(sketch, "E66.top", {"start": v(10.44, -21.08) * mm, "end": v(10.44, -20.32) * mm});
            skLineSegment(sketch, "E66.left", {"start": v(9.68, -21.08) * mm, "end": v(10.44, -21.08) * mm});
            skLineSegment(sketch, "E66.right", {"start": v(9.68, -20.32) * mm, "end": v(10.44, -20.32) * mm});
            skPoint(sketch, "E66.middle", {"position": v(10.06, -20.7) * mm});
            skLineSegment(sketch, "E67.bottom", {"start": v(-29.85, -23.37) * mm, "end": v(-30.6, -23.37) * mm});
            skLineSegment(sketch, "E67.top", {"start": v(-29.85, -22.6) * mm, "end": v(-30.6, -22.6) * mm});
            skLineSegment(sketch, "E67.left", {"start": v(-29.85, -23.37) * mm, "end": v(-29.85, -22.6) * mm});
            skLineSegment(sketch, "E67.right", {"start": v(-30.6, -23.37) * mm, "end": v(-30.6, -22.6) * mm});
            skPoint(sketch, "E67.middle", {"position": v(-30.23, -22.99) * mm});
            skLineSegment(sketch, "E68.bottom", {"start": v(-32.26, -23.37) * mm, "end": v(-33.02, -23.37) * mm});
            skLineSegment(sketch, "E68.top", {"start": v(-32.26, -22.6) * mm, "end": v(-33.02, -22.6) * mm});
            skLineSegment(sketch, "E68.left", {"start": v(-32.26, -23.37) * mm, "end": v(-32.26, -22.6) * mm});
            skLineSegment(sketch, "E68.right", {"start": v(-33.02, -23.37) * mm, "end": v(-33.02, -22.6) * mm});
            skPoint(sketch, "E68.middle", {"position": v(-32.64, -22.99) * mm});
            skLineSegment(sketch, "E69.bottom", {"start": v(-34.67, -23.37) * mm, "end": v(-35.43, -23.37) * mm});
            skLineSegment(sketch, "E69.top", {"start": v(-34.67, -22.6) * mm, "end": v(-35.43, -22.6) * mm});
            skLineSegment(sketch, "E69.left", {"start": v(-34.67, -23.37) * mm, "end": v(-34.67, -22.6) * mm});
            skLineSegment(sketch, "E69.right", {"start": v(-35.43, -23.37) * mm, "end": v(-35.43, -22.6) * mm});
            skPoint(sketch, "E69.middle", {"position": v(-35.05, -22.99) * mm});
            skLineSegment(sketch, "E70.bottom", {"start": v(-29.85, 22.6) * mm, "end": v(-30.6, 22.6) * mm});
            skLineSegment(sketch, "E70.top", {"start": v(-29.85, 23.37) * mm, "end": v(-30.6, 23.37) * mm});
            skLineSegment(sketch, "E70.left", {"start": v(-29.85, 22.6) * mm, "end": v(-29.85, 23.37) * mm});
            skLineSegment(sketch, "E70.right", {"start": v(-30.6, 22.6) * mm, "end": v(-30.6, 23.37) * mm});
            skPoint(sketch, "E70.middle", {"position": v(-30.23, 22.99) * mm});
            skLineSegment(sketch, "E71.bottom", {"start": v(-32.26, 22.6) * mm, "end": v(-33.02, 22.6) * mm});
            skLineSegment(sketch, "E71.top", {"start": v(-32.26, 23.37) * mm, "end": v(-33.02, 23.37) * mm});
            skLineSegment(sketch, "E71.left", {"start": v(-32.26, 22.6) * mm, "end": v(-32.26, 23.37) * mm});
            skLineSegment(sketch, "E71.right", {"start": v(-33.02, 22.6) * mm, "end": v(-33.02, 23.37) * mm});
            skPoint(sketch, "E71.middle", {"position": v(-32.64, 22.99) * mm});
            skLineSegment(sketch, "E72.bottom", {"start": v(-34.67, 22.6) * mm, "end": v(-35.43, 22.6) * mm});
            skLineSegment(sketch, "E72.top", {"start": v(-34.67, 23.37) * mm, "end": v(-35.43, 23.37) * mm});
            skLineSegment(sketch, "E72.left", {"start": v(-34.67, 22.6) * mm, "end": v(-34.67, 23.37) * mm});
            skLineSegment(sketch, "E72.right", {"start": v(-35.43, 22.6) * mm, "end": v(-35.43, 23.37) * mm});
            skPoint(sketch, "E72.middle", {"position": v(-35.05, 22.99) * mm});
            skLineSegment(sketch, "E73.bottom", {"start": v(-32.26, -0.38) * mm, "end": v(-33.02, -0.38) * mm});
            skLineSegment(sketch, "E73.top", {"start": v(-32.26, 0.38) * mm, "end": v(-33.02, 0.38) * mm});
            skLineSegment(sketch, "E73.left", {"start": v(-32.26, -0.38) * mm, "end": v(-32.26, 0.38) * mm});
            skLineSegment(sketch, "E73.right", {"start": v(-33.02, -0.38) * mm, "end": v(-33.02, 0.38) * mm});
            skPoint(sketch, "E73.middle", {"position": v(-32.64, 0) * mm});
            skLineSegment(sketch, "E74.bottom", {"start": v(-34.67, -0.38) * mm, "end": v(-35.43, -0.38) * mm});
            skLineSegment(sketch, "E74.top", {"start": v(-34.67, 0.38) * mm, "end": v(-35.43, 0.38) * mm});
            skLineSegment(sketch, "E74.left", {"start": v(-34.67, -0.38) * mm, "end": v(-34.67, 0.38) * mm});
            skLineSegment(sketch, "E74.right", {"start": v(-35.43, -0.38) * mm, "end": v(-35.43, 0.38) * mm});
            skPoint(sketch, "E74.middle", {"position": v(-35.05, 0) * mm});
            skSolve(sketch);
        }
        {
            var Q0;
            Q0 = qSketchRegion(id + "F3", true);
            extrude(context, id + "F4", {"entities" : qUnion([Q0]), "operationType" : NewBodyOperationType.ADD, "depth" : 7.62 * mm, "offsetDistance" : 25.4 * mm});
        }
        {
            var Q0;
            {var subQ0=sQuery(id+"F2.wireOp",EDGE,"E1.left");Q0=makeQuery(id+"F2.imprint","IMPRINT",FACE,{"disambiguationData":[TD([[makeQuery(id+"F2.imprint","IMPRINT",EDGE,{"derivedFrom":subQ0}),-1.0]])]});}
            var sketch = newSketch(context, id + "F5", { "sketchPlane" : qUnion([Q0])});
            skLineSegment(sketch, "E75.bottom", {"start": v(-29.46, -16) * mm, "end": v(-35.56, -16) * mm});
            skLineSegment(sketch, "E75.top", {"start": v(-29.46, -9.9) * mm, "end": v(-35.56, -9.9) * mm});
            skLineSegment(sketch, "E75.left", {"start": v(-29.46, -16) * mm, "end": v(-29.46, -9.9) * mm});
            skLineSegment(sketch, "E75.right", {"start": v(-35.56, -16) * mm, "end": v(-35.56, -9.9) * mm});
            skPoint(sketch, "E75.middle", {"position": v(-32.51, -12.95) * mm});
            skLineSegment(sketch, "E76.bottom", {"start": v(-29.46, 9.9) * mm, "end": v(-35.56, 9.9) * mm});
            skLineSegment(sketch, "E76.top", {"start": v(-29.46, 16) * mm, "end": v(-35.56, 16) * mm});
            skLineSegment(sketch, "E76.left", {"start": v(-29.46, 9.9) * mm, "end": v(-29.46, 16) * mm});
            skLineSegment(sketch, "E76.right", {"start": v(-35.56, 9.9) * mm, "end": v(-35.56, 16) * mm});
            skPoint(sketch, "E76.middle", {"position": v(-32.51, 12.95) * mm});
            skLineSegment(sketch, "E77.bottom", {"start": v(10.54, 7.24) * mm, "end": v(4.45, 7.24) * mm});
            skLineSegment(sketch, "E77.top", {"start": v(10.54, 13.34) * mm, "end": v(4.45, 13.34) * mm});
            skLineSegment(sketch, "E77.left", {"start": v(10.54, 7.24) * mm, "end": v(10.54, 13.34) * mm});
            skLineSegment(sketch, "E77.right", {"start": v(4.45, 7.24) * mm, "end": v(4.45, 13.34) * mm});
            skPoint(sketch, "E77.middle", {"position": v(7.5, 10.29) * mm});
            skLineSegment(sketch, "E78.bottom", {"start": v(10.54, 17.4) * mm, "end": v(4.45, 17.4) * mm});
            skLineSegment(sketch, "E78.top", {"start": v(10.54, 23.5) * mm, "end": v(4.45, 23.5) * mm});
            skLineSegment(sketch, "E78.left", {"start": v(10.54, 17.4) * mm, "end": v(10.54, 23.5) * mm});
            skLineSegment(sketch, "E78.right", {"start": v(4.45, 17.4) * mm, "end": v(4.45, 23.5) * mm});
            skPoint(sketch, "E78.middle", {"position": v(7.5, 20.45) * mm});
            skLineSegment(sketch, "E79.bottom", {"start": v(38.99, 15.5) * mm, "end": v(33.4, 15.5) * mm});
            skLineSegment(sketch, "E79.top", {"start": v(38.99, 23.11) * mm, "end": v(33.4, 23.11) * mm});
            skLineSegment(sketch, "E79.left", {"start": v(38.99, 15.5) * mm, "end": v(38.99, 23.11) * mm});
            skLineSegment(sketch, "E79.right", {"start": v(33.4, 15.5) * mm, "end": v(33.4, 23.11) * mm});
            skPoint(sketch, "E79.middle", {"position": v(36.2, 19.3) * mm});
            skSolve(sketch);
        }
        {
            var Q0;
            Q0 = qSketchRegion(id + "F5", true);
            extrude(context, id + "F6", {"entities" : qUnion([Q0]), "operationType" : NewBodyOperationType.ADD, "depth" : 3.68 * mm, "offsetDistance" : 25.4 * mm});
        }
        {
            var Q0;
            Q0=makeQuery(id+"F6.opExtrude","CAP_FACE",FACE,{"disambiguationData":[OSD([sQuery(id+"F5.wireOp",EDGE,"E76.bottom"),sQuery(id+"F5.wireOp",EDGE,"E76.top"),sQuery(id+"F5.wireOp",EDGE,"E76.left"),sQuery(id+"F5.wireOp",EDGE,"E76.right")])],"isStart":false});
            var sketch = newSketch(context, id + "F7", { "sketchPlane" : qUnion([Q0])});
            skCircle(sketch, "E80", {"center": v(-32.51, 12.95) * mm, "radius": 1.71 * mm});
            skPoint(sketch, "E80.centerSnap0", {"position": v(-35.56, 12.95) * mm});
            skCircle(sketch, "E81", {"center": v(-32.51, -12.95) * mm, "radius": 1.71 * mm});
            skCircle(sketch, "E82", {"center": v(7.5, 10.29) * mm, "radius": 1.71 * mm});
            skCircle(sketch, "E83", {"center": v(7.5, 20.45) * mm, "radius": 1.71 * mm});
            skSolve(sketch);
        }
        {
            var Q0;
            Q0 = qSketchRegion(id + "F7", true);
            extrude(context, id + "F8", {"entities" : qUnion([Q0]), "operationType" : NewBodyOperationType.ADD, "depth" : 1.4 * mm, "offsetDistance" : 25.4 * mm});
        }
        {
            var Q0;
            Q0=makeQuery(id+"F1.opExtrude","CAP_FACE",FACE,{"disambiguationData":[OSD([sQuery(id+"F0.wireOp",EDGE,"E0.bottom"),sQuery(id+"F0.wireOp",EDGE,"E0.top"),sQuery(id+"F0.wireOp",EDGE,"E0.left"),sQuery(id+"F0.wireOp",EDGE,"E0.right")])],"isStart":true});
            var sketch = newSketch(context, id + "F9", { "sketchPlane" : qUnion([Q0])});
            skLineSegment(sketch, "E84.bottom", {"start": v(-0.74, 18.8) * mm, "end": v(-26.57, 18.8) * mm});
            skLineSegment(sketch, "E84.top", {"start": v(-0.74, 23.75) * mm, "end": v(-26.57, 23.75) * mm});
            skLineSegment(sketch, "E84.left", {"start": v(-0.74, 18.8) * mm, "end": v(-0.74, 23.75) * mm});
            skLineSegment(sketch, "E84.right", {"start": v(-26.57, 18.8) * mm, "end": v(-26.57, 23.75) * mm});
            skPoint(sketch, "E84.middle", {"position": v(-13.65, 21.27) * mm});
            skLineSegment(sketch, "E85.bottom", {"start": v(-0.74, -23.75) * mm, "end": v(-26.57, -23.75) * mm});
            skLineSegment(sketch, "E85.top", {"start": v(-0.74, -18.8) * mm, "end": v(-26.57, -18.8) * mm});
            skLineSegment(sketch, "E85.left", {"start": v(-0.74, -23.75) * mm, "end": v(-0.74, -18.8) * mm});
            skLineSegment(sketch, "E85.right", {"start": v(-26.57, -23.75) * mm, "end": v(-26.57, -18.8) * mm});
            skPoint(sketch, "E85.middle", {"position": v(-13.65, -21.27) * mm});
            skSolve(sketch);
        }
        {
            var Q0;
            Q0 = qSketchRegion(id + "F9", true);
            extrude(context, id + "F10", {"entities" : qUnion([Q0]), "operationType" : NewBodyOperationType.ADD, "depth" : 8.13 * mm, "offsetDistance" : 25.4 * mm});
        }
    });
